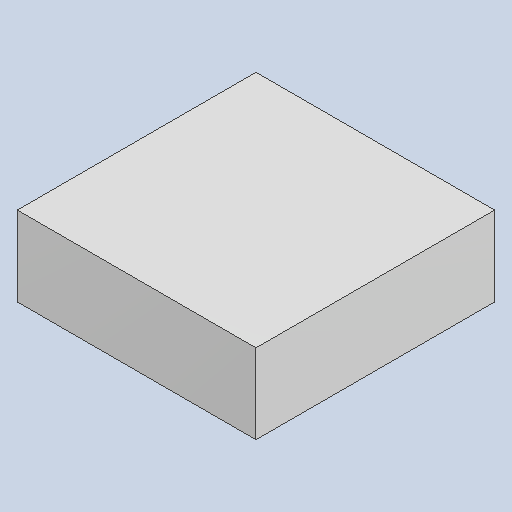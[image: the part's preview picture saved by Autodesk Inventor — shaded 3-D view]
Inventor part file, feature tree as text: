
AUTODESK INVENTOR PART (.ipt)
format: ipt  version: 2023.4 (Build 274418000, 418)  size: 79,872 bytes
history: native  units: mm
features: extrude x1
ambient origin geometry x8: Origin, YZ Plane, XZ Plane, XY Plane, X Axis, Y Axis, Z Axis, Center Point
bodies: Solid1 (feature_tree)
feature tree (1):
  extrude  "Extruded_12"  [1 undecoded]
note: 1 required parameter value undecoded (feature->parameter linkage not recoverable at this tier; creation-order binding heuristic only, values carry confidence <= 0.55)
